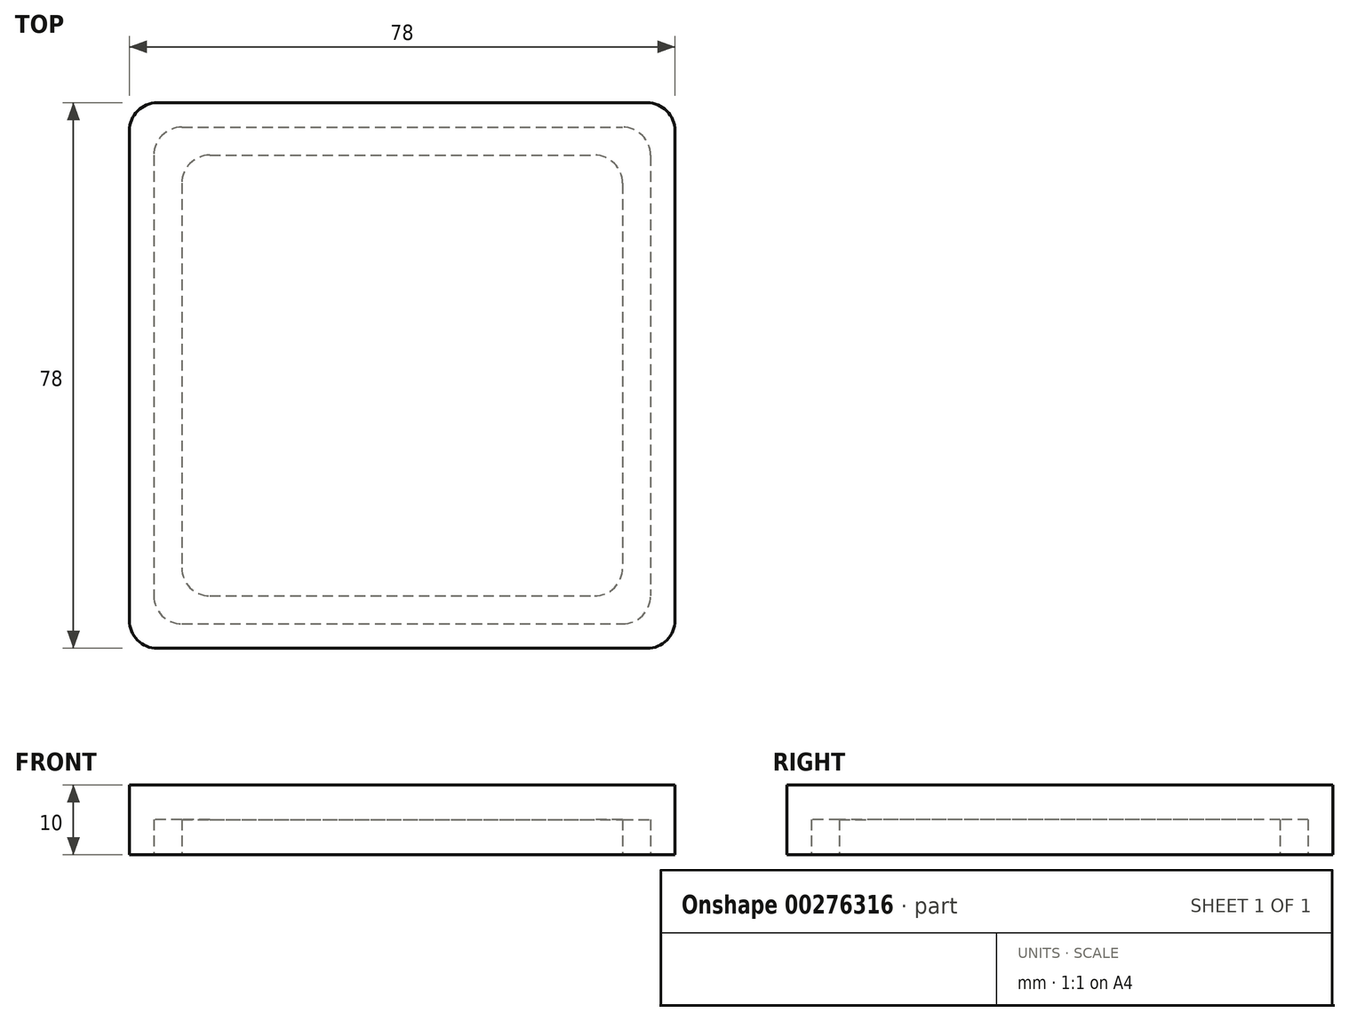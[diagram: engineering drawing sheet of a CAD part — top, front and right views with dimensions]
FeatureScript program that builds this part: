
annotation { "Feature Type Name" : "Feature", "Feature Type Description" : "" }
export const myFeature = defineFeature(function(context is Context, id is Id, definition is map)
    precondition{}
    {
        {
            var Q0;
            Q0=qCreatedBy(makeId("Top.planeOp"),FACE);
            var sketch = newSketch(context, id + "F0", { "sketchPlane" : qUnion([Q0])});
            skLineSegment(sketch, "E0.bottom", {"start": v(-20.5, 38.5) * mm, "end": v(34.5, 38.5) * mm});
            skLineSegment(sketch, "E0.top", {"start": v(-20.5, -24.5) * mm, "end": v(34.5, -24.5) * mm});
            skLineSegment(sketch, "E0.left", {"start": v(-24.5, 34.5) * mm, "end": v(-24.5, -20.5) * mm});
            skLineSegment(sketch, "E0.right", {"start": v(38.5, 34.5) * mm, "end": v(38.5, -20.5) * mm});
            skLineSegment(sketch, "E1.bottom", {"start": v(-24.5, 42.5) * mm, "end": v(38.5, 42.5) * mm});
            skLineSegment(sketch, "E1.top", {"start": v(-24.5, -28.5) * mm, "end": v(38.5, -28.5) * mm});
            skLineSegment(sketch, "E1.left", {"start": v(-28.5, 38.5) * mm, "end": v(-28.5, -24.5) * mm});
            skLineSegment(sketch, "E1.right", {"start": v(42.5, 38.5) * mm, "end": v(42.5, -24.5) * mm});
            skLineSegment(sketch, "E2.bottom", {"start": v(-28, 46) * mm, "end": v(42, 46) * mm});
            skLineSegment(sketch, "E2.top", {"start": v(-28, -32) * mm, "end": v(42, -32) * mm});
            skLineSegment(sketch, "E2.left", {"start": v(-32, 42) * mm, "end": v(-32, -28) * mm});
            skLineSegment(sketch, "E2.right", {"start": v(46, 42) * mm, "end": v(46, -28) * mm});
            skPoint(sketch, "E3.visualSharp", {"position": v(-24.5, 38.5) * mm});
            skArc(sketch, "E3.filletArc", {"start": v(-20.5, 38.5) * mm, "mid": v(-23.33, 37.33) * mm, "end": v(-24.5, 34.5) * mm});
            skPoint(sketch, "E4.visualSharp", {"position": v(-28.5, 42.5) * mm});
            skArc(sketch, "E4.filletArc", {"start": v(-24.5, 42.5) * mm, "mid": v(-27.33, 41.33) * mm, "end": v(-28.5, 38.5) * mm});
            skPoint(sketch, "E5.visualSharp", {"position": v(38.5, 38.5) * mm});
            skArc(sketch, "E5.filletArc", {"start": v(38.5, 34.5) * mm, "mid": v(37.33, 37.33) * mm, "end": v(34.5, 38.5) * mm});
            skPoint(sketch, "E6.visualSharp", {"position": v(42.5, 42.5) * mm});
            skArc(sketch, "E6.filletArc", {"start": v(42.5, 38.5) * mm, "mid": v(41.33, 41.33) * mm, "end": v(38.5, 42.5) * mm});
            skPoint(sketch, "E7.visualSharp", {"position": v(46, 46) * mm});
            skArc(sketch, "E7.filletArc", {"start": v(46, 42) * mm, "mid": v(44.83, 44.83) * mm, "end": v(42, 46) * mm});
            skPoint(sketch, "E8.visualSharp", {"position": v(-32, 46) * mm});
            skArc(sketch, "E8.filletArc", {"start": v(-28, 46) * mm, "mid": v(-30.83, 44.83) * mm, "end": v(-32, 42) * mm});
            skPoint(sketch, "E9.visualSharp", {"position": v(-32, -32) * mm});
            skArc(sketch, "E9.filletArc", {"start": v(-32, -28) * mm, "mid": v(-30.83, -30.83) * mm, "end": v(-28, -32) * mm});
            skPoint(sketch, "E10.visualSharp", {"position": v(-24.5, -24.5) * mm});
            skArc(sketch, "E10.filletArc", {"start": v(-24.5, -20.5) * mm, "mid": v(-23.33, -23.33) * mm, "end": v(-20.5, -24.5) * mm});
            skPoint(sketch, "E11.visualSharp", {"position": v(46, -32) * mm});
            skArc(sketch, "E11.filletArc", {"start": v(42, -32) * mm, "mid": v(44.83, -30.83) * mm, "end": v(46, -28) * mm});
            skPoint(sketch, "E12.visualSharp", {"position": v(38.5, -24.5) * mm});
            skArc(sketch, "E12.filletArc", {"start": v(34.5, -24.5) * mm, "mid": v(37.33, -23.33) * mm, "end": v(38.5, -20.5) * mm});
            skPoint(sketch, "E13.visualSharp", {"position": v(-28.5, -28.5) * mm});
            skArc(sketch, "E13.filletArc", {"start": v(-28.5, -24.5) * mm, "mid": v(-27.33, -27.33) * mm, "end": v(-24.5, -28.5) * mm});
            skPoint(sketch, "E14.visualSharp", {"position": v(42.5, -28.5) * mm});
            skArc(sketch, "E14.filletArc", {"start": v(38.5, -28.5) * mm, "mid": v(41.33, -27.33) * mm, "end": v(42.5, -24.5) * mm});
            skLineSegment(sketch, "E15", {"start": v(-67.98, 7) * mm, "end": v(64.23, 7) * mm, "construction": true});
            skLineSegment(sketch, "E16", {"start": v(7, 52.66) * mm, "end": v(7, -52.26) * mm, "construction": true});
            skLineSegment(sketch, "E17.bottom", {"start": v(3, 11) * mm, "end": v(11, 11) * mm});
            skLineSegment(sketch, "E17.top", {"start": v(3, 3) * mm, "end": v(11, 3) * mm});
            skLineSegment(sketch, "E17.left", {"start": v(3, 11) * mm, "end": v(3, 3) * mm});
            skLineSegment(sketch, "E17.right", {"start": v(11, 11) * mm, "end": v(11, 3) * mm});
            skSolve(sketch);
        }
        {
            var Q0;
            Q0=makeQuery(id+"F0.imprint","IMPRINT",FACE,{"disambiguationData":[TD([[makeQuery(id+"F0.imprint","IMPRINT",EDGE,{"derivedFrom":sQuery(id+"F0.wireOp",EDGE,"E1.bottom")}),1.0]])]});
            var Q1;
            Q1=makeQuery(id+"F0.imprint","IMPRINT",FACE,{"disambiguationData":[TD([[makeQuery(id+"F0.imprint","IMPRINT",EDGE,{"derivedFrom":sQuery(id+"F0.wireOp",EDGE,"E0.bottom")}),1.0]])]});
            var Q2;
            Q2=makeQuery(id+"F0.imprint","IMPRINT",FACE,{"disambiguationData":[TD([[makeQuery(id+"F0.imprint","IMPRINT",EDGE,{"derivedFrom":sQuery(id+"F0.wireOp",EDGE,"E0.bottom")}),-1.0]])]});
            var Q3;
            Q3=makeQuery(id+"F0.imprint","IMPRINT",FACE,{"disambiguationData":[TD([[makeQuery(id+"F0.imprint","IMPRINT",EDGE,{"derivedFrom":sQuery(id+"F0.wireOp",EDGE,"E17.bottom")}),-1.0]])]});
            extrude(context, id + "F1", {"entities" : qUnion([Q0, Q1, Q2, Q3]), "depth" : 10 * mm});
        }
        {
            var Q0;
            Q0=makeQuery(id+"F0.imprint","IMPRINT",FACE,{"disambiguationData":[TD([[makeQuery(id+"F0.imprint","IMPRINT",EDGE,{"derivedFrom":sQuery(id+"F0.wireOp",EDGE,"E0.bottom")}),1.0]])]});
            extrude(context, id + "F2", {"entities" : qUnion([Q0]), "operationType" : NewBodyOperationType.REMOVE, "depth" : 5 * mm});
        }
    });
